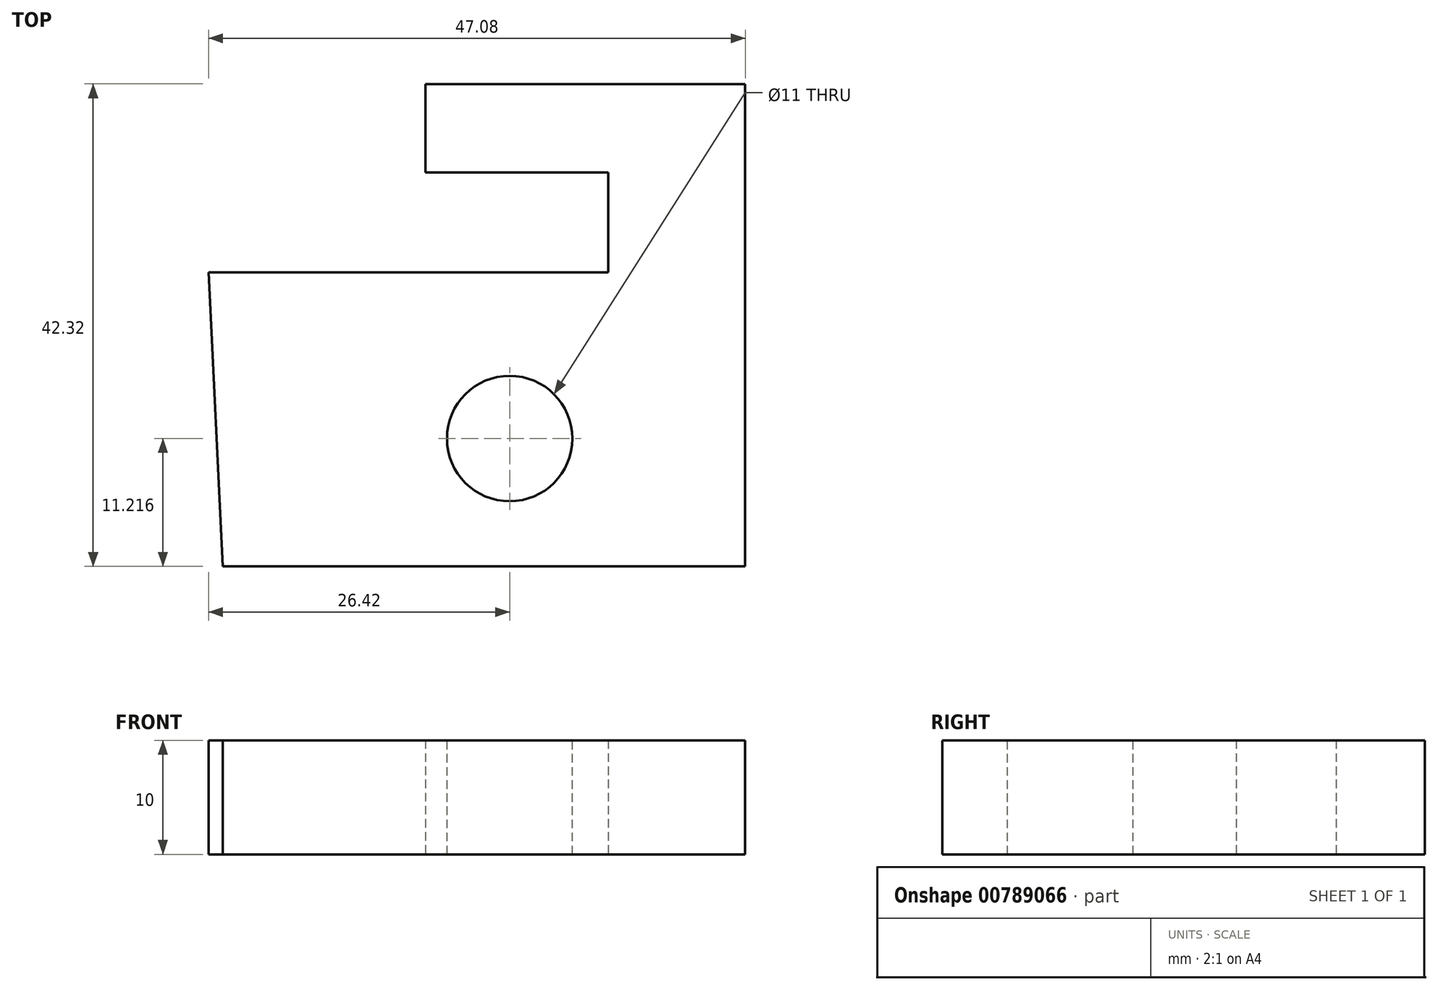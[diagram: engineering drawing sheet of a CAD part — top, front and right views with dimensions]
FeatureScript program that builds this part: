
annotation { "Feature Type Name" : "Feature", "Feature Type Description" : "" }
export const myFeature = defineFeature(function(context is Context, id is Id, definition is map)
    precondition{}
    {
        {
            var Q0;
            Q0=qCreatedBy(makeId("Top.planeOp"),FACE);
            var sketch = newSketch(context, id + "F0", { "sketchPlane" : qUnion([Q0])});
            skLineSegment(sketch, "E0", {"start": v(-25.16, -25.8) * mm, "end": v(20.66, -25.8) * mm});
            skLineSegment(sketch, "E1", {"start": v(20.66, -25.8) * mm, "end": v(20.66, 16.53) * mm});
            skLineSegment(sketch, "E2", {"start": v(20.66, 16.53) * mm, "end": v(-7.39, 16.53) * mm});
            skLineSegment(sketch, "E3", {"start": v(-7.39, 16.53) * mm, "end": v(-7.39, 8.76) * mm});
            skLineSegment(sketch, "E4", {"start": v(-7.39, 8.76) * mm, "end": v(8.64, 8.76) * mm});
            skLineSegment(sketch, "E5", {"start": v(8.64, 8.76) * mm, "end": v(8.64, 0) * mm});
            skLineSegment(sketch, "E6", {"start": v(8.64, 0) * mm, "end": v(0, 0) * mm});
            skLineSegment(sketch, "E7", {"start": v(0, 0) * mm, "end": v(-26.42, 0) * mm});
            skLineSegment(sketch, "E8", {"start": v(-26.42, 0) * mm, "end": v(-25.16, -25.8) * mm});
            skSolve(sketch);
        }
        {
            var Q0;
            Q0 = qSketchRegion(id + "F0", true);
            extrude(context, id + "F1", {"entities" : qUnion([Q0]), "depth" : 10 * mm, "offsetDistance" : 25 * mm});
        }
        {
            var Q0;
            Q0=makeQuery(id+"F1.opExtrude","CAP_FACE",FACE,{"disambiguationData":[OSD([sQuery(id+"F0.wireOp",EDGE,"E0"),sQuery(id+"F0.wireOp",EDGE,"E1"),sQuery(id+"F0.wireOp",EDGE,"E2"),sQuery(id+"F0.wireOp",EDGE,"E3"),sQuery(id+"F0.wireOp",EDGE,"E4"),sQuery(id+"F0.wireOp",EDGE,"E5"),sQuery(id+"F0.wireOp",EDGE,"E6"),sQuery(id+"F0.wireOp",EDGE,"E7"),sQuery(id+"F0.wireOp",EDGE,"E8")])],"isStart":false});
            var sketch = newSketch(context, id + "F2", { "sketchPlane" : qUnion([Q0])});
            skCircle(sketch, "E9", {"center": v(0, -14.57) * mm, "radius": 4.45 * mm});
            skSolve(sketch);
        }
        {
            var Q0;
            Q0=sQuery(id+"F2.wireOp",VERTEX,"E9.center");
            var Q1;
            Q1=makeQuery(id+"F1.opExtrude","SWEPT_BODY",BODY,{"disambiguationData":[OSD([sQuery(id+"F0.wireOp",EDGE,"E0"),sQuery(id+"F0.wireOp",EDGE,"E1"),sQuery(id+"F0.wireOp",EDGE,"E2"),sQuery(id+"F0.wireOp",EDGE,"E3"),sQuery(id+"F0.wireOp",EDGE,"E4"),sQuery(id+"F0.wireOp",EDGE,"E5"),sQuery(id+"F0.wireOp",EDGE,"E6"),sQuery(id+"F0.wireOp",EDGE,"E7"),sQuery(id+"F0.wireOp",EDGE,"E8")])]});
            hole(context, id + "F3", {"style" : HoleStyle.SIMPLE, "endStyle" : HoleEndStyle.THROUGH, "holeDiameter" : 11 * mm, "majorDiameter" : 5 * mm, "isTappedThrough" : true, "tappedDepth" : 12 * mm, "tapClearance" : 3, "locations" : qUnion([Q0]), "scope" : qUnion([Q1])});
        }
    });
